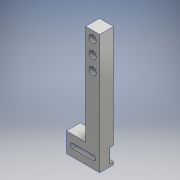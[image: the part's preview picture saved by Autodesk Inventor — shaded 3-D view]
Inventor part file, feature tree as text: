
AUTODESK INVENTOR PART (.ipt)
format: ipt  version: 2016 (Build 200138000, 138)  size: 158,720 bytes
history: native  units: mm
features: extrude x5, sketch x4, mirror x1
ambient origin geometry x8: Origin, YZ Plane, XZ Plane, XY Plane, X Axis, Y Axis, Z Axis, Center Point
bodies: Solid1 (feature_tree)
feature tree (10):
  extrude  "Extrusion1"  Depth=108.0mm
  extrude  "Extrusion2"  Depth=90.2mm
  extrude  "Extrusion3"  Depth=12.8mm
  sketch  "Sketch4"  dims[d7=3.5mm d8=0.0mm d9=4.0mm d10=4.0mm d11=3.5mm d12=0.0mm d13=11.0mm d14=11.0mm d15=11.0mm d16=12.5mm d17=12.5mm d18=6.5mm d19=6.5mm d20=6.5mm d21=3.5mm d22=0.0mm d23=6.0mm d24=0.0mm d25=6.5mm]
  extrude  "Extrusion4"  Depth=4.0mm
  extrude  "Extrusion5"  Depth=4.0mm
  mirror  "Mirror1"
  sketch  "Sketch1"  dims[d0=30.0mm d1=108.0mm]
  sketch  "Sketch2"  dims[d2=12.7mm d3=90.2mm]
  sketch  "Sketch3"  dims[d4=12.5mm d5=0.0mm d6=12.8mm]
